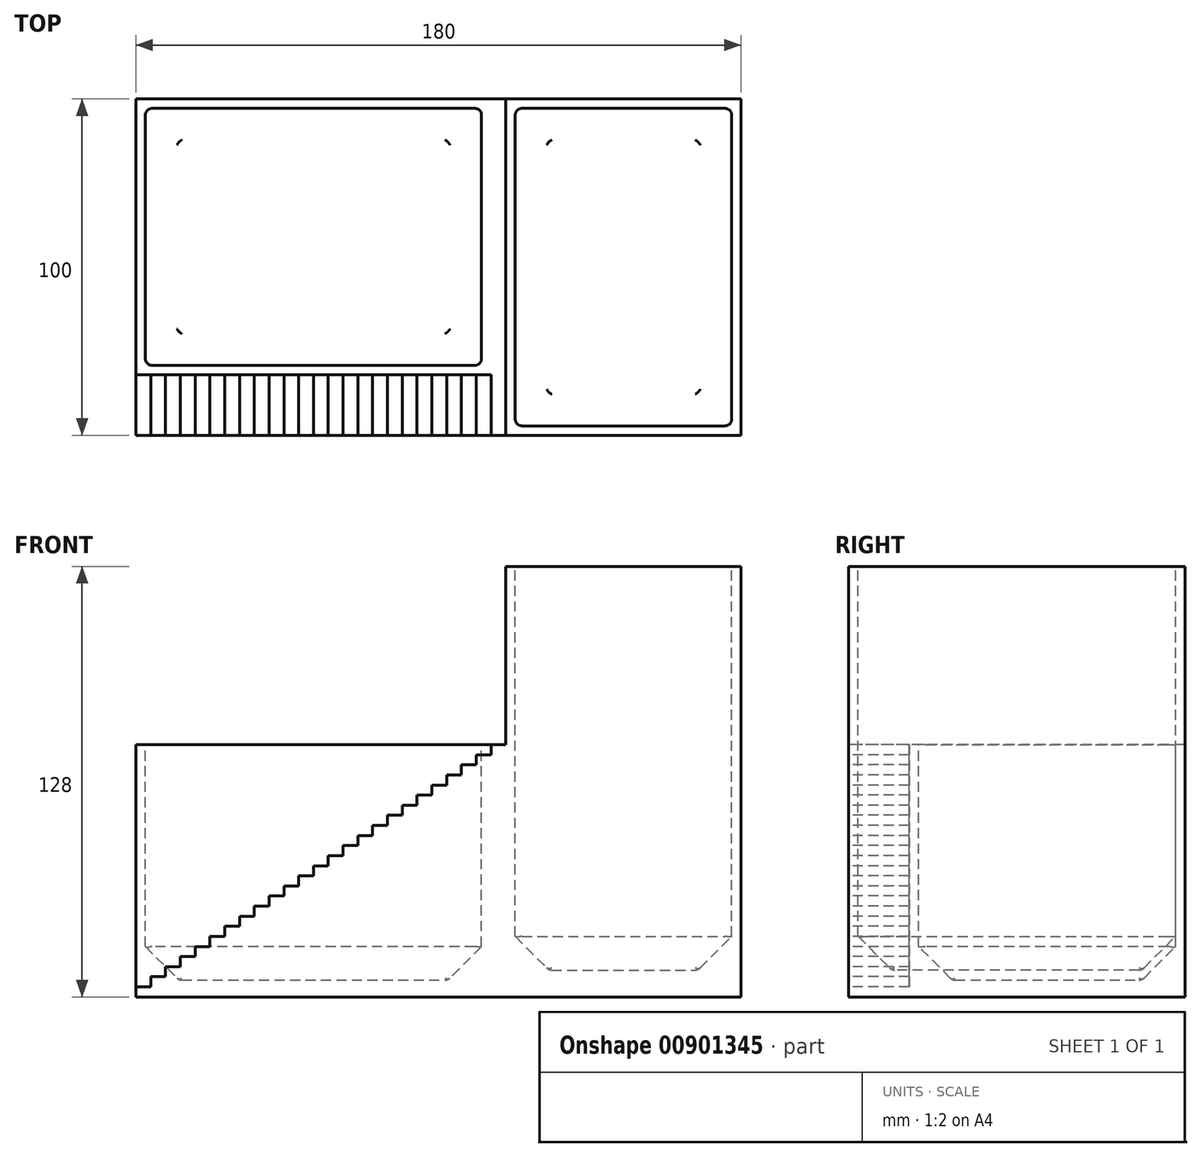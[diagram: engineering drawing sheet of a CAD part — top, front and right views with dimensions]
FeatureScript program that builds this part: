
annotation { "Feature Type Name" : "Feature", "Feature Type Description" : "" }
export const myFeature = defineFeature(function(context is Context, id is Id, definition is map)
    precondition{}
    {
        {
            var Q0;
            Q0=qCreatedBy(makeId("Top.planeOp"),FACE);
            var sketch = newSketch(context, id + "F0", { "sketchPlane" : qUnion([Q0])});
            skLineSegment(sketch, "E0.bottom", {"start": v(-90, -50) * mm, "end": v(90, -50) * mm});
            skLineSegment(sketch, "E0.top", {"start": v(-90, 50) * mm, "end": v(90, 50) * mm});
            skLineSegment(sketch, "E0.left", {"start": v(-90, -50) * mm, "end": v(-90, 50) * mm});
            skLineSegment(sketch, "E0.right", {"start": v(90, -50) * mm, "end": v(90, 50) * mm});
            skPoint(sketch, "E0.middle", {"position": v(0, 0) * mm});
            skSolve(sketch);
        }
        {
            var Q0;
            Q0=makeQuery(id+"F0.imprint","IMPRINT",FACE,{"disambiguationData":[TD([[makeQuery(id+"F0.imprint","IMPRINT",EDGE,{"derivedFrom":sQuery(id+"F0.wireOp",EDGE,"E0.bottom")}),1.0]])]});
            extrude(context, id + "F1", {"entities" : qUnion([Q0]), "depth" : 128 * mm, "offsetDistance" : 25 * mm});
        }
        {
            var Q0;
            Q0=makeQuery(id+"F1.opExtrude","SWEPT_FACE",FACE,{"disambiguationData":[OSD([sQuery(id+"F0.wireOp",EDGE,"E0.bottom")])]});
            var sketch = newSketch(context, id + "F2", { "sketchPlane" : qUnion([Q0])});
            skLineSegment(sketch, "E1.bottom", {"start": v(-90, 128) * mm, "end": v(20, 128) * mm});
            skLineSegment(sketch, "E1.top", {"start": v(-90, 75) * mm, "end": v(20, 75) * mm});
            skLineSegment(sketch, "E1.left", {"start": v(-90, 128) * mm, "end": v(-90, 75) * mm});
            skLineSegment(sketch, "E1.right", {"start": v(20, 128) * mm, "end": v(20, 75) * mm});
            skLineSegment(sketch, "E2", {"start": v(-90, 0) * mm, "end": v(20, 75) * mm, "construction": true});
            skLineSegment(sketch, "E3", {"start": v(-90, 0) * mm, "end": v(-90, 3) * mm});
            skLineSegment(sketch, "E4", {"start": v(-90, 3) * mm, "end": v(-85.6, 3) * mm});
            skLineSegment(sketch, "E5", {"start": v(-85.6, 3) * mm, "end": v(-85.6, 6) * mm});
            skLineSegment(sketch, "E6", {"start": v(-85.6, 6) * mm, "end": v(-81.2, 6) * mm});
            skLineSegment(sketch, "E7", {"start": v(-81.2, 6) * mm, "end": v(-81.2, 9) * mm});
            skLineSegment(sketch, "E8", {"start": v(-81.2, 9) * mm, "end": v(-76.8, 9) * mm});
            skLineSegment(sketch, "E9", {"start": v(-76.8, 9) * mm, "end": v(-76.8, 12) * mm});
            skLineSegment(sketch, "E10", {"start": v(-76.8, 12) * mm, "end": v(-72.4, 12) * mm});
            skLineSegment(sketch, "E11", {"start": v(-72.4, 12) * mm, "end": v(-72.4, 15) * mm});
            skLineSegment(sketch, "E12", {"start": v(-72.4, 15) * mm, "end": v(-68, 15) * mm});
            skLineSegment(sketch, "E13", {"start": v(-68, 15) * mm, "end": v(-68, 18) * mm});
            skLineSegment(sketch, "E14", {"start": v(-68, 18) * mm, "end": v(-63.6, 18) * mm});
            skLineSegment(sketch, "E15", {"start": v(-63.6, 18) * mm, "end": v(-63.6, 21) * mm});
            skLineSegment(sketch, "E16", {"start": v(-63.6, 21) * mm, "end": v(-59.2, 21) * mm});
            skLineSegment(sketch, "E17", {"start": v(-59.2, 21) * mm, "end": v(-59.2, 24) * mm});
            skLineSegment(sketch, "E18", {"start": v(-59.2, 24) * mm, "end": v(-54.8, 24) * mm});
            skLineSegment(sketch, "E19", {"start": v(-54.8, 24) * mm, "end": v(-54.8, 27) * mm});
            skLineSegment(sketch, "E20", {"start": v(-54.8, 27) * mm, "end": v(-50.4, 27) * mm});
            skLineSegment(sketch, "E21", {"start": v(-50.4, 27) * mm, "end": v(-50.4, 30) * mm});
            skLineSegment(sketch, "E22", {"start": v(-50.4, 30) * mm, "end": v(-46, 30) * mm});
            skLineSegment(sketch, "E23", {"start": v(-46, 30) * mm, "end": v(-46, 33) * mm});
            skLineSegment(sketch, "E24", {"start": v(-46, 33) * mm, "end": v(-41.6, 33) * mm});
            skLineSegment(sketch, "E25", {"start": v(-41.6, 33) * mm, "end": v(-41.6, 36) * mm});
            skLineSegment(sketch, "E26", {"start": v(-41.6, 36) * mm, "end": v(-37.2, 36) * mm});
            skLineSegment(sketch, "E27", {"start": v(-37.2, 36) * mm, "end": v(-37.2, 39) * mm});
            skLineSegment(sketch, "E28", {"start": v(-37.2, 39) * mm, "end": v(-32.8, 39) * mm});
            skLineSegment(sketch, "E29", {"start": v(-32.8, 39) * mm, "end": v(-32.8, 42) * mm});
            skLineSegment(sketch, "E30", {"start": v(-32.8, 42) * mm, "end": v(-28.4, 42) * mm});
            skLineSegment(sketch, "E31", {"start": v(-28.4, 42) * mm, "end": v(-28.4, 45) * mm});
            skLineSegment(sketch, "E32", {"start": v(-28.4, 45) * mm, "end": v(-24, 45) * mm});
            skLineSegment(sketch, "E33", {"start": v(-24, 45) * mm, "end": v(-24, 48) * mm});
            skLineSegment(sketch, "E34", {"start": v(-24, 48) * mm, "end": v(-19.6, 48) * mm});
            skLineSegment(sketch, "E35", {"start": v(-19.6, 48) * mm, "end": v(-19.6, 51) * mm});
            skLineSegment(sketch, "E36", {"start": v(-19.6, 51) * mm, "end": v(-15.2, 51) * mm});
            skLineSegment(sketch, "E37", {"start": v(-15.2, 51) * mm, "end": v(-15.2, 54) * mm});
            skLineSegment(sketch, "E38", {"start": v(-15.2, 54) * mm, "end": v(-10.8, 54) * mm});
            skLineSegment(sketch, "E39", {"start": v(-10.8, 54) * mm, "end": v(-10.8, 57) * mm});
            skLineSegment(sketch, "E40", {"start": v(-10.8, 57) * mm, "end": v(-6.4, 57) * mm});
            skLineSegment(sketch, "E41", {"start": v(-6.4, 57) * mm, "end": v(-6.4, 60) * mm});
            skLineSegment(sketch, "E42", {"start": v(-6.4, 60) * mm, "end": v(-2, 60) * mm});
            skLineSegment(sketch, "E43", {"start": v(-2, 60) * mm, "end": v(-2, 63) * mm});
            skLineSegment(sketch, "E44", {"start": v(-2, 63) * mm, "end": v(2.4, 63) * mm});
            skLineSegment(sketch, "E45", {"start": v(2.4, 63) * mm, "end": v(2.4, 63) * mm});
            skLineSegment(sketch, "E46", {"start": v(2.4, 63) * mm, "end": v(2.4, 66) * mm});
            skLineSegment(sketch, "E47", {"start": v(2.4, 66) * mm, "end": v(6.8, 66) * mm});
            skLineSegment(sketch, "E48", {"start": v(6.8, 66) * mm, "end": v(6.8, 69) * mm});
            skLineSegment(sketch, "E49", {"start": v(6.8, 69) * mm, "end": v(11.2, 69) * mm});
            skLineSegment(sketch, "E50", {"start": v(11.2, 69) * mm, "end": v(11.2, 72) * mm});
            skLineSegment(sketch, "E51", {"start": v(11.2, 72) * mm, "end": v(15.6, 72) * mm});
            skLineSegment(sketch, "E52", {"start": v(15.6, 72) * mm, "end": v(15.6, 75) * mm});
            skLineSegment(sketch, "E53", {"start": v(15.6, 75) * mm, "end": v(20, 75) * mm});
            skLineSegment(sketch, "E54", {"start": v(20, 75) * mm, "end": v(20, 78) * mm});
            skSolve(sketch);
        }
        {
            var Q0;
            {var subQ6=sQuery(id+"F2.wireOp",EDGE,"E1.bottom");Q0=makeQuery(id+"F2.imprint","IMPRINT",FACE,{"disambiguationData":[TD([[makeQuery(id+"F2.imprint","IMPRINT",EDGE,{"derivedFrom":subQ6}),-1.0]])]});}
            extrude(context, id + "F3", {"entities" : qUnion([Q0]), "operationType" : NewBodyOperationType.REMOVE, "endBound" : BoundingType.UP_TO_NEXT, "oppositeDirection" : true, "depth" : 25 * mm, "offsetDistance" : 25 * mm});
        }
        {
            var Q0;
            {var subQ4=sQuery(id+"F2.wireOp",EDGE,"E4");Q0=makeQuery(id+"F2.imprint","IMPRINT",FACE,{"disambiguationData":[TD([[makeQuery(id+"F2.imprint","IMPRINT",EDGE,{"derivedFrom":subQ4}),1.0]])]});}
            extrude(context, id + "F4", {"entities" : qUnion([Q0]), "operationType" : NewBodyOperationType.REMOVE, "oppositeDirection" : true, "depth" : 18 * mm, "offsetDistance" : 25 * mm});
        }
        {
            var Q0;
            Q0=makeQuery(id+"F3.boolean.opBoolean","COPY",FACE,{"derivedFrom":makeQuery(id+"F3.opExtrude","SWEPT_FACE",FACE,{"disambiguationData":[OSD([sQuery(id+"F2.wireOp",EDGE,"E1.top")])]})});
            var sketch = newSketch(context, id + "F5", { "sketchPlane" : qUnion([Q0])});
            skLineSegment(sketch, "E55.bottom", {"start": v(-90, -32) * mm, "end": v(15.6, -32) * mm, "construction": true});
            skLineSegment(sketch, "E55.top", {"start": v(-90, 50) * mm, "end": v(15.6, 50) * mm, "construction": true});
            skLineSegment(sketch, "E55.left", {"start": v(-90, -32) * mm, "end": v(-90, 50) * mm, "construction": true});
            skLineSegment(sketch, "E55.right", {"start": v(15.6, -32) * mm, "end": v(15.6, 50) * mm, "construction": true});
            skLineSegment(sketch, "E56.0", {"start": v(12.8, -29.2) * mm, "end": v(12.8, 47.2) * mm});
            skLineSegment(sketch, "E56.1", {"start": v(-87.2, -29.2) * mm, "end": v(12.8, -29.2) * mm});
            skLineSegment(sketch, "E56.2", {"start": v(-87.2, -29.2) * mm, "end": v(-87.2, 47.2) * mm});
            skLineSegment(sketch, "E56.3", {"start": v(-87.2, 47.2) * mm, "end": v(12.8, 47.2) * mm});
            skSolve(sketch);
        }
        {
            var Q0;
            Q0=makeQuery(id+"F5.imprint","IMPRINT",FACE,{"disambiguationData":[TD([[makeQuery(id+"F5.imprint","IMPRINT",EDGE,{"derivedFrom":sQuery(id+"F5.wireOp",EDGE,"E56.0")}),1.0]])]});
            extrude(context, id + "F6", {"entities" : qUnion([Q0]), "operationType" : NewBodyOperationType.REMOVE, "oppositeDirection" : true, "depth" : 70 * mm, "offsetDistance" : 25 * mm});
        }
        {
            var Q0;
            Q0=makeQuery(id+"F1.opExtrude","CAP_FACE",FACE,{"disambiguationData":[OSD([sQuery(id+"F0.wireOp",EDGE,"E0.bottom"),sQuery(id+"F0.wireOp",EDGE,"E0.top"),sQuery(id+"F0.wireOp",EDGE,"E0.left"),sQuery(id+"F0.wireOp",EDGE,"E0.right")])],"isStart":false});
            var sketch = newSketch(context, id + "F7", { "sketchPlane" : qUnion([Q0])});
            skLineSegment(sketch, "E57.0", {"start": v(22.8, 47.2) * mm, "end": v(22.8, -47.2) * mm});
            skLineSegment(sketch, "E57.1", {"start": v(22.8, 47.2) * mm, "end": v(87.2, 47.2) * mm});
            skLineSegment(sketch, "E57.2", {"start": v(87.2, -47.2) * mm, "end": v(87.2, 47.2) * mm});
            skLineSegment(sketch, "E57.3", {"start": v(22.8, -47.2) * mm, "end": v(87.2, -47.2) * mm});
            skLineSegment(sketch, "E58.0", {"start": v(22.55, 47.2) * mm, "end": v(22.55, -47.2) * mm});
            skSolve(sketch);
        }
        {
            var Q0;
            Q0=makeQuery(id+"F7.imprint","IMPRINT",FACE,{"disambiguationData":[TD([[makeQuery(id+"F7.imprint","IMPRINT",EDGE,{"derivedFrom":sQuery(id+"F7.wireOp",EDGE,"E57.0")}),1.0]])]});
            extrude(context, id + "F8", {"entities" : qUnion([Q0]), "operationType" : NewBodyOperationType.REMOVE, "oppositeDirection" : true, "depth" : 120 * mm, "offsetDistance" : 25 * mm});
        }
        {
            var Q0;
            Q0=makeQuery(id+"F8.boolean.opBoolean","COPY",FACE,{"derivedFrom":makeQuery(id+"F8.opExtrude","CAP_FACE",FACE,{"disambiguationData":[OSD([sQuery(id+"F7.wireOp",EDGE,"E57.0"),sQuery(id+"F7.wireOp",EDGE,"E57.1"),sQuery(id+"F7.wireOp",EDGE,"E57.2"),sQuery(id+"F7.wireOp",EDGE,"E57.3")])],"isStart":false})});
            var Q1;
            Q1=makeQuery(id+"F6.boolean.opBoolean","COPY",FACE,{"derivedFrom":makeQuery(id+"F6.opExtrude","CAP_FACE",FACE,{"disambiguationData":[OSD([sQuery(id+"F5.wireOp",EDGE,"E56.0"),sQuery(id+"F5.wireOp",EDGE,"E56.1"),sQuery(id+"F5.wireOp",EDGE,"E56.2"),sQuery(id+"F5.wireOp",EDGE,"E56.3")])],"isStart":false})});
            chamfer(context, id + "F9", {"entities" : qUnion([Q0, Q1]), "width" : 10 * mm, "tangentPropagation" : true});
        }
        {
            var Q0;
            Q0=makeQuery(id+"F6.boolean.opBoolean","COPY",EDGE,{"derivedFrom":makeQuery(id+"F6.opExtrude","SWEPT_EDGE",EDGE,{"disambiguationData":[OSD([sQuery(id+"F5.wireOp",EDGE,"E56.0"),sQuery(id+"F5.wireOp",EDGE,"E56.1")])]})});
            var Q1;
            Q1=makeQuery(id+"F9.opChamfer","BLEND_EDGE",EDGE,{"blendedFrom":[makeQuery(id+"F6.boolean.opBoolean","COPY",EDGE,{"derivedFrom":makeQuery(id+"F6.opExtrude","CAP_EDGE",EDGE,{"disambiguationData":[OSD([sQuery(id+"F5.wireOp",EDGE,"E56.0")])],"isStart":false})}),makeQuery(id+"F6.boolean.opBoolean","COPY",EDGE,{"derivedFrom":makeQuery(id+"F6.opExtrude","CAP_EDGE",EDGE,{"disambiguationData":[OSD([sQuery(id+"F5.wireOp",EDGE,"E56.1")])],"isStart":false})})],"blendedInto":[]});
            var Q2;
            Q2=makeQuery(id+"F9.opChamfer","BLEND_EDGE",EDGE,{"blendedFrom":[makeQuery(id+"F6.boolean.opBoolean","COPY",EDGE,{"derivedFrom":makeQuery(id+"F6.opExtrude","CAP_EDGE",EDGE,{"disambiguationData":[OSD([sQuery(id+"F5.wireOp",EDGE,"E56.0")])],"isStart":false})}),makeQuery(id+"F6.boolean.opBoolean","COPY",EDGE,{"derivedFrom":makeQuery(id+"F6.opExtrude","CAP_EDGE",EDGE,{"disambiguationData":[OSD([sQuery(id+"F5.wireOp",EDGE,"E56.3")])],"isStart":false})})],"blendedInto":[]});
            var Q3;
            Q3=makeQuery(id+"F6.boolean.opBoolean","COPY",EDGE,{"derivedFrom":makeQuery(id+"F6.opExtrude","SWEPT_EDGE",EDGE,{"disambiguationData":[OSD([sQuery(id+"F5.wireOp",EDGE,"E56.0"),sQuery(id+"F5.wireOp",EDGE,"E56.3")])]})});
            var Q4;
            Q4=makeQuery(id+"F6.boolean.opBoolean","COPY",EDGE,{"derivedFrom":makeQuery(id+"F6.opExtrude","SWEPT_EDGE",EDGE,{"disambiguationData":[OSD([sQuery(id+"F5.wireOp",EDGE,"E56.2"),sQuery(id+"F5.wireOp",EDGE,"E56.3")])]})});
            var Q5;
            Q5=makeQuery(id+"F9.opChamfer","BLEND_EDGE",EDGE,{"blendedFrom":[makeQuery(id+"F6.boolean.opBoolean","COPY",EDGE,{"derivedFrom":makeQuery(id+"F6.opExtrude","CAP_EDGE",EDGE,{"disambiguationData":[OSD([sQuery(id+"F5.wireOp",EDGE,"E56.2")])],"isStart":false})}),makeQuery(id+"F6.boolean.opBoolean","COPY",EDGE,{"derivedFrom":makeQuery(id+"F6.opExtrude","CAP_EDGE",EDGE,{"disambiguationData":[OSD([sQuery(id+"F5.wireOp",EDGE,"E56.3")])],"isStart":false})})],"blendedInto":[]});
            var Q6;
            Q6=makeQuery(id+"F9.opChamfer","BLEND_EDGE",EDGE,{"blendedFrom":[makeQuery(id+"F6.boolean.opBoolean","COPY",EDGE,{"derivedFrom":makeQuery(id+"F6.opExtrude","CAP_EDGE",EDGE,{"disambiguationData":[OSD([sQuery(id+"F5.wireOp",EDGE,"E56.1")])],"isStart":false})}),makeQuery(id+"F6.boolean.opBoolean","COPY",EDGE,{"derivedFrom":makeQuery(id+"F6.opExtrude","CAP_EDGE",EDGE,{"disambiguationData":[OSD([sQuery(id+"F5.wireOp",EDGE,"E56.2")])],"isStart":false})})],"blendedInto":[]});
            var Q7;
            Q7=makeQuery(id+"F6.boolean.opBoolean","COPY",EDGE,{"derivedFrom":makeQuery(id+"F6.opExtrude","SWEPT_EDGE",EDGE,{"disambiguationData":[OSD([sQuery(id+"F5.wireOp",EDGE,"E56.1"),sQuery(id+"F5.wireOp",EDGE,"E56.2")])]})});
            var Q8;
            Q8=makeQuery(id+"F8.boolean.opBoolean","COPY",EDGE,{"derivedFrom":makeQuery(id+"F8.opExtrude","SWEPT_EDGE",EDGE,{"disambiguationData":[OSD([sQuery(id+"F7.wireOp",EDGE,"E57.0"),sQuery(id+"F7.wireOp",EDGE,"E57.3")])]})});
            var Q9;
            Q9=makeQuery(id+"F9.opChamfer","BLEND_EDGE",EDGE,{"blendedFrom":[makeQuery(id+"F8.boolean.opBoolean","COPY",EDGE,{"derivedFrom":makeQuery(id+"F8.opExtrude","CAP_EDGE",EDGE,{"disambiguationData":[OSD([sQuery(id+"F7.wireOp",EDGE,"E57.0")])],"isStart":false})}),makeQuery(id+"F8.boolean.opBoolean","COPY",EDGE,{"derivedFrom":makeQuery(id+"F8.opExtrude","CAP_EDGE",EDGE,{"disambiguationData":[OSD([sQuery(id+"F7.wireOp",EDGE,"E57.3")])],"isStart":false})})],"blendedInto":[]});
            var Q10;
            Q10=makeQuery(id+"F8.boolean.opBoolean","COPY",EDGE,{"derivedFrom":makeQuery(id+"F8.opExtrude","SWEPT_EDGE",EDGE,{"disambiguationData":[OSD([sQuery(id+"F7.wireOp",EDGE,"E57.2"),sQuery(id+"F7.wireOp",EDGE,"E57.3")])]})});
            var Q11;
            Q11=makeQuery(id+"F9.opChamfer","BLEND_EDGE",EDGE,{"blendedFrom":[makeQuery(id+"F8.boolean.opBoolean","COPY",EDGE,{"derivedFrom":makeQuery(id+"F8.opExtrude","CAP_EDGE",EDGE,{"disambiguationData":[OSD([sQuery(id+"F7.wireOp",EDGE,"E57.2")])],"isStart":false})}),makeQuery(id+"F8.boolean.opBoolean","COPY",EDGE,{"derivedFrom":makeQuery(id+"F8.opExtrude","CAP_EDGE",EDGE,{"disambiguationData":[OSD([sQuery(id+"F7.wireOp",EDGE,"E57.3")])],"isStart":false})})],"blendedInto":[]});
            var Q12;
            Q12=makeQuery(id+"F9.opChamfer","BLEND_EDGE",EDGE,{"blendedFrom":[makeQuery(id+"F8.boolean.opBoolean","COPY",EDGE,{"derivedFrom":makeQuery(id+"F8.opExtrude","CAP_EDGE",EDGE,{"disambiguationData":[OSD([sQuery(id+"F7.wireOp",EDGE,"E57.1")])],"isStart":false})}),makeQuery(id+"F8.boolean.opBoolean","COPY",EDGE,{"derivedFrom":makeQuery(id+"F8.opExtrude","CAP_EDGE",EDGE,{"disambiguationData":[OSD([sQuery(id+"F7.wireOp",EDGE,"E57.2")])],"isStart":false})})],"blendedInto":[]});
            var Q13;
            Q13=makeQuery(id+"F8.boolean.opBoolean","COPY",EDGE,{"derivedFrom":makeQuery(id+"F8.opExtrude","SWEPT_EDGE",EDGE,{"disambiguationData":[OSD([sQuery(id+"F7.wireOp",EDGE,"E57.1"),sQuery(id+"F7.wireOp",EDGE,"E57.2")])]})});
            var Q14;
            Q14=makeQuery(id+"F9.opChamfer","BLEND_EDGE",EDGE,{"blendedFrom":[makeQuery(id+"F8.boolean.opBoolean","COPY",EDGE,{"derivedFrom":makeQuery(id+"F8.opExtrude","CAP_EDGE",EDGE,{"disambiguationData":[OSD([sQuery(id+"F7.wireOp",EDGE,"E57.0")])],"isStart":false})}),makeQuery(id+"F8.boolean.opBoolean","COPY",EDGE,{"derivedFrom":makeQuery(id+"F8.opExtrude","CAP_EDGE",EDGE,{"disambiguationData":[OSD([sQuery(id+"F7.wireOp",EDGE,"E57.1")])],"isStart":false})})],"blendedInto":[]});
            var Q15;
            Q15=makeQuery(id+"F8.boolean.opBoolean","COPY",EDGE,{"derivedFrom":makeQuery(id+"F8.opExtrude","SWEPT_EDGE",EDGE,{"disambiguationData":[OSD([sQuery(id+"F7.wireOp",EDGE,"E57.0"),sQuery(id+"F7.wireOp",EDGE,"E57.1")])]})});
            var Q16;
            Q16=makeQuery(id+"F8.boolean.opBoolean","COPY",FACE,{"derivedFrom":makeQuery(id+"F8.opExtrude","CAP_FACE",FACE,{"disambiguationData":[OSD([sQuery(id+"F7.wireOp",EDGE,"E57.0"),sQuery(id+"F7.wireOp",EDGE,"E57.1"),sQuery(id+"F7.wireOp",EDGE,"E57.2"),sQuery(id+"F7.wireOp",EDGE,"E57.3")])],"isStart":false})});
            var Q17;
            Q17=makeQuery(id+"F6.boolean.opBoolean","COPY",FACE,{"derivedFrom":makeQuery(id+"F6.opExtrude","CAP_FACE",FACE,{"disambiguationData":[OSD([sQuery(id+"F5.wireOp",EDGE,"E56.0"),sQuery(id+"F5.wireOp",EDGE,"E56.1"),sQuery(id+"F5.wireOp",EDGE,"E56.2"),sQuery(id+"F5.wireOp",EDGE,"E56.3")])],"isStart":false})});
            fillet(context, id + "F10", {"entities" : qUnion([Q0, Q1, Q2, Q3, Q4, Q5, Q6, Q7, Q8, Q9, Q10, Q11, Q12, Q13, Q14, Q15, Q16, Q17]), "radius" : 2 * mm, "tangentPropagation" : true, "allowEdgeOverflow" : false});
        }
    });
